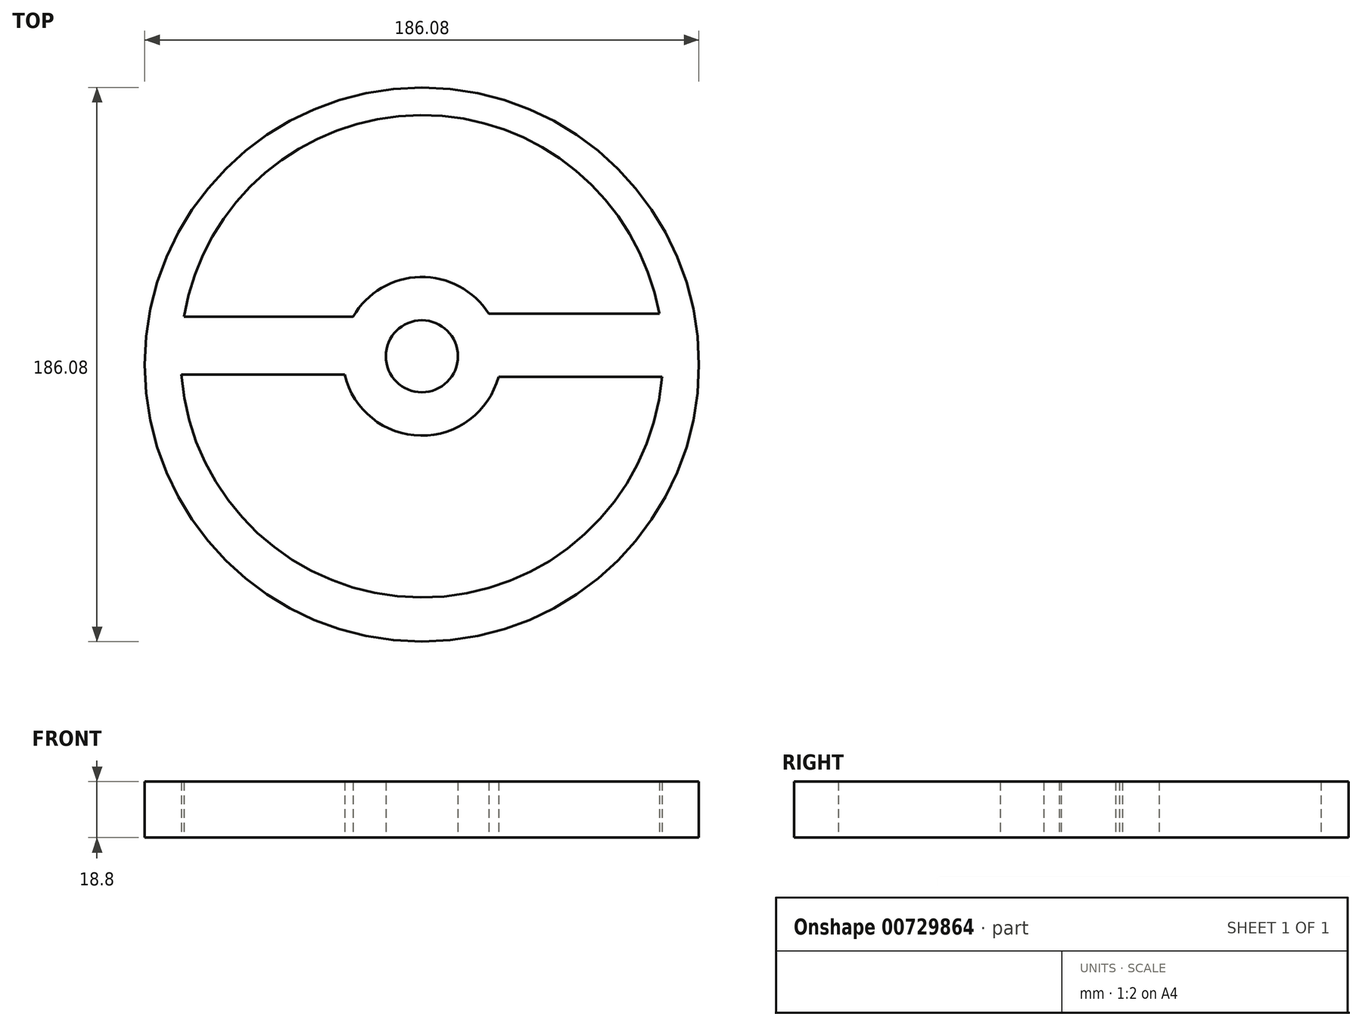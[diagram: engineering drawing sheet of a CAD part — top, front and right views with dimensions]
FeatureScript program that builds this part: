
annotation { "Feature Type Name" : "Feature", "Feature Type Description" : "" }
export const myFeature = defineFeature(function(context is Context, id is Id, definition is map)
    precondition{}
    {
        {
            var Q0;
            Q0=qCreatedBy(makeId("Top.planeOp"),FACE);
            var sketch = newSketch(context, id + "F0", { "sketchPlane" : qUnion([Q0])});
            skCircle(sketch, "E0", {"center": v(0, -2.8) * mm, "radius": 93.04 * mm});
            skCircle(sketch, "E1", {"center": v(0, 0) * mm, "radius": 12.1 * mm});
            skCircle(sketch, "E2", {"center": v(0, 0) * mm, "radius": 26.64 * mm});
            skCircle(sketch, "E3", {"center": v(0, 0) * mm, "radius": 6.3 * mm});
            skCircle(sketch, "E4", {"center": v(0, 0) * mm, "radius": 20.27 * mm});
            skCircle(sketch, "E5", {"center": v(0, 0) * mm, "radius": 81 * mm});
            skLineSegment(sketch, "E6", {"start": v(-79.89, 13.35) * mm, "end": v(-23.06, 13.35) * mm});
            skLineSegment(sketch, "E7", {"start": v(-80.76, -6.18) * mm, "end": v(-25.92, -6.18) * mm});
            skLineSegment(sketch, "E8", {"start": v(79.89, 14.33) * mm, "end": v(22.46, 14.33) * mm});
            skLineSegment(sketch, "E9", {"start": v(80.7, -6.9) * mm, "end": v(25.74, -6.9) * mm});
            skSolve(sketch);
        }
        {
            var Q0;
            Q0 = qSketchRegion(id + "F0", true);
            var Q1;
            Q1=makeQuery(id+"F0.imprint","IMPRINT",FACE,{"disambiguationData":[TD([[makeQuery(id+"F0.imprint","IMPRINT",EDGE,{"derivedFrom":sQuery(id+"F0.wireOp",EDGE,"E1")}),-1.0]])]});
            var Q2;
            {var subQ3=sQuery(id+"F0.wireOp",EDGE,"E9");Q2=makeQuery(id+"F0.imprint","IMPRINT",FACE,{"disambiguationData":[TD([[makeQuery(id+"F0.imprint","IMPRINT",EDGE,{"derivedFrom":subQ3}),-1.0]])]});}
            var Q3;
            {var subQ0=sQuery(id+"F0.wireOp",EDGE,"E6");Q3=makeQuery(id+"F0.imprint","IMPRINT",FACE,{"disambiguationData":[TD([[makeQuery(id+"F0.imprint","IMPRINT",EDGE,{"derivedFrom":subQ0}),-1.0]])]});}
            var Q4;
            Q4=makeQuery(id+"F0.imprint","IMPRINT",FACE,{"disambiguationData":[TD([[makeQuery(id+"F0.imprint","IMPRINT",EDGE,{"derivedFrom":sQuery(id+"F0.wireOp",EDGE,"E4")}),-1.0]])]});
            extrude(context, id + "F1", {"entities" : qUnion([Q0, Q1, Q2, Q3, Q4]), "depth" : 18.8 * mm, "offsetDistance" : 25.4 * mm});
        }
    });
